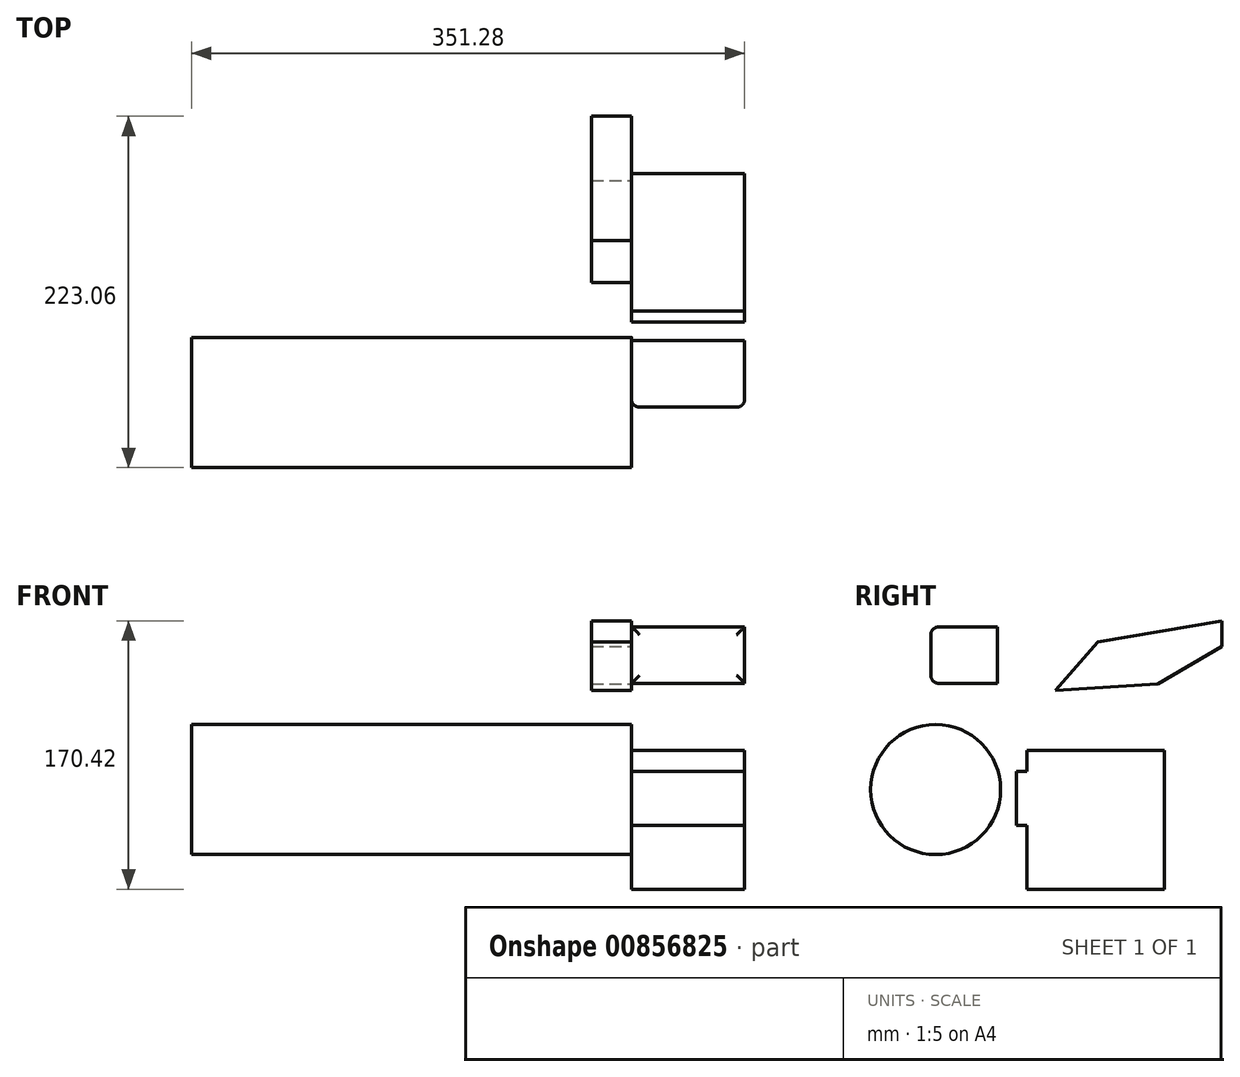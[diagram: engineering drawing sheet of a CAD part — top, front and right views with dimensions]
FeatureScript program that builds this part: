
annotation { "Feature Type Name" : "Feature", "Feature Type Description" : "" }
export const myFeature = defineFeature(function(context is Context, id is Id, definition is map)
    precondition{}
    {
        {
            var Q0;
            Q0=qCreatedBy(makeId("Right.planeOp"),FACE);
            var sketch = newSketch(context, id + "F0", { "sketchPlane" : qUnion([Q0])});
            skLineSegment(sketch, "E0.bottom", {"start": v(-44.9, 47.65) * mm, "end": v(42.4, 47.65) * mm});
            skLineSegment(sketch, "E0.top", {"start": v(-44.9, -40.64) * mm, "end": v(42.4, -40.64) * mm});
            skLineSegment(sketch, "E0.left", {"start": v(-44.9, 47.65) * mm, "end": v(-44.9, -40.64) * mm});
            skLineSegment(sketch, "E0.right", {"start": v(42.4, 47.65) * mm, "end": v(42.4, -40.64) * mm});
            skLineSegment(sketch, "E1.bottom", {"start": v(0, 0) * mm, "end": v(-51.76, 0) * mm});
            skLineSegment(sketch, "E1.top", {"start": v(0, 34.16) * mm, "end": v(-51.76, 34.16) * mm});
            skLineSegment(sketch, "E1.left", {"start": v(0, 0) * mm, "end": v(0, 34.16) * mm});
            skLineSegment(sketch, "E1.right", {"start": v(-51.76, 0) * mm, "end": v(-51.76, 34.16) * mm});
            skLineSegment(sketch, "E2.bottom", {"start": v(-106.01, 126.1) * mm, "end": v(-63.6, 126.1) * mm});
            skLineSegment(sketch, "E2.top", {"start": v(-106.01, 90.13) * mm, "end": v(-63.6, 90.13) * mm});
            skLineSegment(sketch, "E2.left", {"start": v(-106.01, 126.1) * mm, "end": v(-106.01, 90.13) * mm});
            skLineSegment(sketch, "E2.right", {"start": v(-63.6, 126.1) * mm, "end": v(-63.6, 90.13) * mm});
            skSolve(sketch);
        }
        {
            var Q0;
            Q0 = qSketchRegion(id + "F0", true);
            extrude(context, id + "F1", {"entities" : qUnion([Q0]), "depth" : 71.88 * mm, "offsetDistance" : 25.4 * mm});
        }
        {
            var Q0;
            Q0=makeQuery(id+"F1.opExtrude","SWEPT_FACE",FACE,{"disambiguationData":[OSD([sQuery(id+"F0.wireOp",EDGE,"E2.left")])]});
            fillet(context, id + "F2", {"entities" : qUnion([Q0]), "radius" : 5.08 * mm, "tangentPropagation" : true, "allowEdgeOverflow" : false});
        }
        {
            var Q0;
            Q0=qCreatedBy(makeId("Right.planeOp"),FACE);
            var sketch = newSketch(context, id + "F3", { "sketchPlane" : qUnion([Q0])});
            skLineSegment(sketch, "E3", {"start": v(0, 70.76) * mm, "end": v(72.17, 70.76) * mm});
            skLineSegment(sketch, "E4", {"start": v(78.8, 113.55) * mm, "end": v(78.8, 129.78) * mm});
            skLineSegment(sketch, "E5", {"start": v(78.8, 129.78) * mm, "end": v(0, 116.32) * mm});
            skLineSegment(sketch, "E6", {"start": v(0, 116.32) * mm, "end": v(-26.8, 85.76) * mm});
            skLineSegment(sketch, "E7", {"start": v(-26.8, 85.76) * mm, "end": v(38.08, 89.77) * mm});
            skLineSegment(sketch, "E8", {"start": v(38.08, 89.77) * mm, "end": v(78.8, 113.55) * mm});
            skCircle(sketch, "E9", {"center": v(-102.98, 22.69) * mm, "radius": 41.29 * mm});
            skSolve(sketch);
        }
        {
            var Q0;
            Q0=makeQuery(id+"F3.imprint","IMPRINT",FACE,{"disambiguationData":[TD([[makeQuery(id+"F3.imprint","IMPRINT",EDGE,{"derivedFrom":sQuery(id+"F3.wireOp",EDGE,"E4")}),1.0]])]});
            var Q1;
            Q1=makeQuery(id+"F3.imprint","IMPRINT",FACE,{"disambiguationData":[TD([[makeQuery(id+"F3.imprint","IMPRINT",EDGE,{"derivedFrom":sQuery(id+"F3.wireOp",EDGE,"E9")}),1.0]])]});
            extrude(context, id + "F4", {"entities" : qUnion([Q0, Q1]), "oppositeDirection" : true, "depth" : 25.4 * mm, "offsetDistance" : 25.4 * mm});
        }
        {
            var Q0;
            Q0=makeQuery(id+"F4.opExtrude","CAP_FACE",FACE,{"disambiguationData":[OSD([sQuery(id+"F3.wireOp",EDGE,"E9")])],"isStart":false});
            extrude(context, id + "F5", {"entities" : qUnion([Q0]), "operationType" : NewBodyOperationType.ADD, "depth" : 254 * mm, "offsetDistance" : 25.4 * mm});
        }
    });
